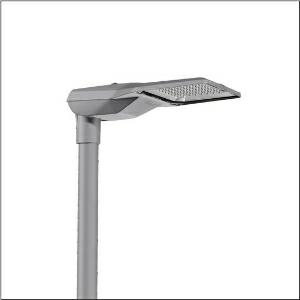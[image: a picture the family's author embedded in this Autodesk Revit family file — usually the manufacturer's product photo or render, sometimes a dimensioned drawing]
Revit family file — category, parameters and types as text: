
# Revit family: streetlight_sl_21_midi___st0_8a_5xe3c33s08mb_531e
name_source: partatom
category: Lighting Fixtures
units: mm (PartAtom-declared; Revit-internal decimal feet)

## family parameters
Cut with Voids When Loaded = No
Host = Face
Light Source = No
Part Type = Normal
Room Calculation Point = No
Round Connector Dimension = Use Diameter
Shared = No

## types (1)
- --- (1 x LED, 18270 lm, 136 W, 3000K)
    Apparent Load = 136 VA
    CIE Flux Codes = 38 75 97 100 100
    Color Rendering = 70
    Color Temperature = 3000K
    Default Elevation = 1800 mm
    Description = Streetlight SL 21 midi, mast luminaire, primary light control with lens, of PMMA, primary optical cover: cover, of toughened safety glass, transparent, light distribution: ST0.8a, light emission: direct distribution, primary light characteristic: asymmetric, installation type: side-entry, post-top, LED, High Power LED, rated luminous flux: 18.270lm, luminous efficacy: 134lm/W, light colour: 730, colour temperature: 3000K, control gear: D4i, control: overheat protection, constant luminous flux control, time-dependent luminous flux control, flexible luminous flux parameterisation, pre-setting: logarithmic dimming characteristic, mains connection: 230..240V, AC, 50/60Hz, start of lifetime: 136W, end of service life: 142W, reduction: 61W, luminaire housing, of diecast aluminium, powder-coated, SITECO metallic grey (DB 702S), corrosivity category C5 high according to DIN EN ISO 12944, please order mast flange separately, inclination adjustable: 0°, 5°, 10°, 15°, sealing non-destructively replaceable, multi-level sealing system, length: 644mm, width: 335mm, height: 110mm, mast flange for spigot size: 42mm (side-entry): 5XC10008XM4, 60/48mm (side-entry/post-top): 5XC10108XM2, 76/60mm (side-entry/post-top): 5XC10108XM1, mounting height: 4..8m, Smart Interface above, protection rating (complete): IP66, insulation class (complete): insulation class II (safety insulation), certification: CE, ENEC, ENEC+, VDE, impact resistance: IK10, permissible operating ambient temperature for outdoor applications: -40..+50°C, standard-compliant lighting for roads and squares, packaging unit: 1 piece

Light Distribution: ST0.8a
    Height = 111 mm
    Lamp = 1 x LED
    Lamp Light Flux = 18270 lm
    Lamp Power = 136 W
    Lamp count = 1
    Length = 644 mm
    Luminous efficacy = 134 lm/W
    Manufacturer = Siteco
    ModVariant = No
    Model = 5XE3C33S08MB
    Number of Poles = 1
    OnlyDefault = Yes
    Power Factor = 1
    Product Name = Streetlight SL 21 midi | ST0.8a
    Product group = mast luminaire | pylon top
    ProductGroupID = 6100
    Protection Class = Protection class II
    Protection Degree = IP 66
    RLX_Detail_Level = 1
    RLX_Emergency_Light_Flux = 0 lm
    RLX_Emergency_Type = 0
    RLX_Emergency_Type_DB = No
    RlxData = <blob elided: 26913 chars, md5=db7f8126>
    Socket = socket
    Standby Power = 0 W
    System Light Flux = 18270 lm
    System Power = 136 W
    Type Comments = factory setting: luminous flux: 100 % | dim-lin: 254 | 695 mA
    Type Image = l_1004302.jpg
    URL = http://relux.com
    VarID = @adj_183569
    Voltage = 0 V
    Weight = 0.00 kg
    Width = 336 mm

## geometry (parser evidence)
native form markers: Blend x4, Sweep x9
no freeform markers — native parametric forms only
